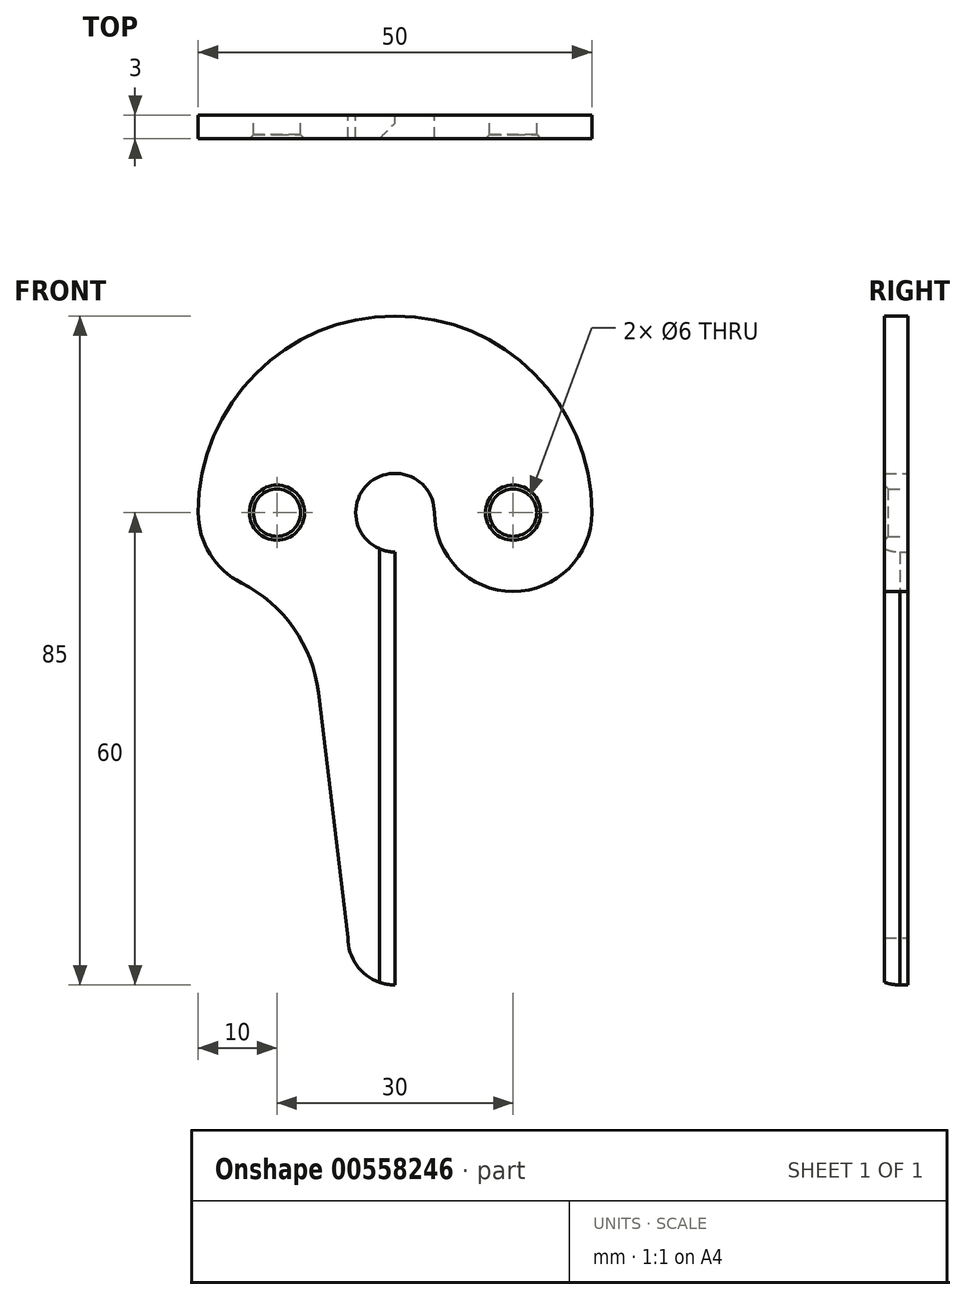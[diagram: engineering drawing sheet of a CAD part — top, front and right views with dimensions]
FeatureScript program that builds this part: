
annotation { "Feature Type Name" : "Feature", "Feature Type Description" : "" }
export const myFeature = defineFeature(function(context is Context, id is Id, definition is map)
    precondition{}
    {
        {
            var Q0;
            Q0=qCreatedBy(makeId("Front.planeOp"),FACE);
            var sketch = newSketch(context, id + "F0", { "sketchPlane" : qUnion([Q0])});
            skPoint(sketch, "E0", {"position": v(0, 0) * mm});
            skPoint(sketch, "E1", {"position": v(0, -54) * mm});
            skPoint(sketch, "E2", {"position": v(-15, 0) * mm});
            skPoint(sketch, "E3", {"position": v(15, 0) * mm});
            skCircle(sketch, "E4", {"center": v(-15, 0) * mm, "radius": 3 * mm});
            skCircle(sketch, "E5", {"center": v(15, 0) * mm, "radius": 3 * mm});
            skArc(sketch, "E6", {"start": v(5, 0) * mm, "mid": v(-3.54, 3.54) * mm, "end": v(0, -5) * mm});
            skPoint(sketch, "E7", {"position": v(-27.6, -25) * mm});
            skArc(sketch, "E8", {"start": v(-6, -54) * mm, "mid": v(-4.24, -58.24) * mm, "end": v(0, -60) * mm});
            skArc(sketch, "E9", {"start": v(-9.74, -22.86) * mm, "mid": v(-12.87, -14.67) * mm, "end": v(-19.5, -8.93) * mm});
            skLineSegment(sketch, "E10", {"start": v(-6, -54) * mm, "end": v(-9.68, -23.36) * mm});
            skLineSegment(sketch, "E11", {"start": v(0, -60) * mm, "end": v(0, -5) * mm});
            skArc(sketch, "E12", {"start": v(5, 0) * mm, "mid": v(15, -10) * mm, "end": v(25, 0) * mm});
            skArc(sketch, "E13.trimOffspring", {"start": v(25, 0) * mm, "mid": v(0, 25) * mm, "end": v(-25, 0) * mm});
            skArc(sketch, "E14", {"start": v(-25, 0) * mm, "mid": v(-23.52, -5.24) * mm, "end": v(-19.5, -8.93) * mm});
            skLineSegment(sketch, "E15", {"start": v(-9.68, -23.36) * mm, "end": v(-9.74, -22.86) * mm});
            skSolve(sketch);
        }
        {
            var Q0;
            Q0=makeQuery(id+"F0.imprint","IMPRINT",FACE,{"disambiguationData":[TD([[makeQuery(id+"F0.imprint","IMPRINT",EDGE,{"derivedFrom":sQuery(id+"F0.wireOp",EDGE,"E4")}),-1.0]])]});
            extrude(context, id + "F1", {"entities" : qUnion([Q0]), "depth" : 3 * mm});
        }
        {
            var Q0;
            Q0=makeQuery(id+"F1.opExtrude","CAP_EDGE",EDGE,{"disambiguationData":[OSD([sQuery(id+"F0.wireOp",EDGE,"E11")])],"isStart":false});
            chamfer(context, id + "F2", {"entities" : qUnion([Q0]), "width" : 2 * mm, "tangentPropagation" : true});
        }
        {
            var Q0;
            Q0=makeQuery(id+"F1.opExtrude","CAP_EDGE",EDGE,{"disambiguationData":[OSD([sQuery(id+"F0.wireOp",EDGE,"E4")])],"isStart":false});
            var Q1;
            Q1=makeQuery(id+"F1.opExtrude","CAP_EDGE",EDGE,{"disambiguationData":[OSD([sQuery(id+"F0.wireOp",EDGE,"E5")])],"isStart":false});
            chamfer(context, id + "F3", {"entities" : qUnion([Q0, Q1]), "width" : 0.5 * mm, "tangentPropagation" : true});
        }
    });
